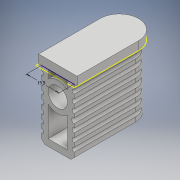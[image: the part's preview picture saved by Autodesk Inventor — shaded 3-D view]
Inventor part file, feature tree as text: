
AUTODESK INVENTOR PART (.ipt)
format: ipt  version: 2018 (Build 220112000, 112)  size: 246,272 bytes
history: native  units: mm
features: extrude x5, sketch x5, projected_geometry x3, chamfer x2, mirror x1
ambient origin geometry x8: Origin, YZ Plane, XZ Plane, XY Plane, X Axis, Y Axis, Z Axis, Center Point
bodies: Solid1 (feature_tree)
feature tree (16):
  extrude  "Extrusion1"  Depth=11.5mm
  extrude  "Extrusion2"  Depth=19.5mm
  extrude  "Extrusion3"  Depth=11.5mm
  extrude  "Extrusion4"  Depth=11.5mm
  mirror  "Mirror1"
  chamfer  "Chamfer1"  Distance=40.0mm
  chamfer  "Chamfer2"  Distance=5.0mm
  extrude  "Extrusion5"  Depth=5.0mm
  sketch  "Sketch1"  dims[d0=38.5mm d1=11.5mm]
  sketch  "Sketch2"  dims[d2=5.0mm d3=0.0mm d4=19.5mm]
  projected_geometry  "Projected Loop1"
  sketch  "Sketch3"  dims[d5=40.0mm d6=0.0mm d8=11.5mm]
  projected_geometry  "Projected Loop2"
  sketch  "Sketch4"  dims[d9=3.0mm d10=11.5mm d11=40.0mm d12=0.0mm]
  projected_geometry  "Projected Loop3"
  sketch  "Sketch5"  dims[d13=17.0mm d14=5.0mm d15=5.0mm d16=5.0mm d17=5.0mm d18=5.0mm d19=5.0mm d20=40.0mm d21=0.0mm d22=2.0mm d23=2.0mm d24=45.0deg d25=4.0mm d26=2.0mm d27=45.0deg d28=40.0mm d29=0.0mm d31=4.0mm d32=4.0mm d33=4.0mm]
